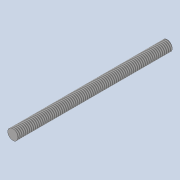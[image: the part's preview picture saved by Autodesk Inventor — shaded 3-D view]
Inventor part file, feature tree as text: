
AUTODESK INVENTOR PART (.ipt)
format: ipt  version: 2020 (Build 240168000, 168)  size: 107,520 bytes
history: native  units: mm
features: extrude x1, thread x1, sketch x1
ambient origin geometry x8: Origin, YZ Plane, XZ Plane, XY Plane, X Axis, Y Axis, Z Axis, Center Point
bodies: Solid1 (feature_tree)
feature tree (3):
  extrude  "Extrusion1"  Depth=120.0mm TaperAngle=0.0deg
  thread  "Thread1"  [1 undecoded]
  sketch  "Sketch1"  dims[d0=8.0mm d1=120.0mm d2=0.0mm d3=550.0mm d4=0.0mm]
note: 1 required parameter value undecoded (feature->parameter linkage not recoverable at this tier; creation-order binding heuristic only, values carry confidence <= 0.55)
